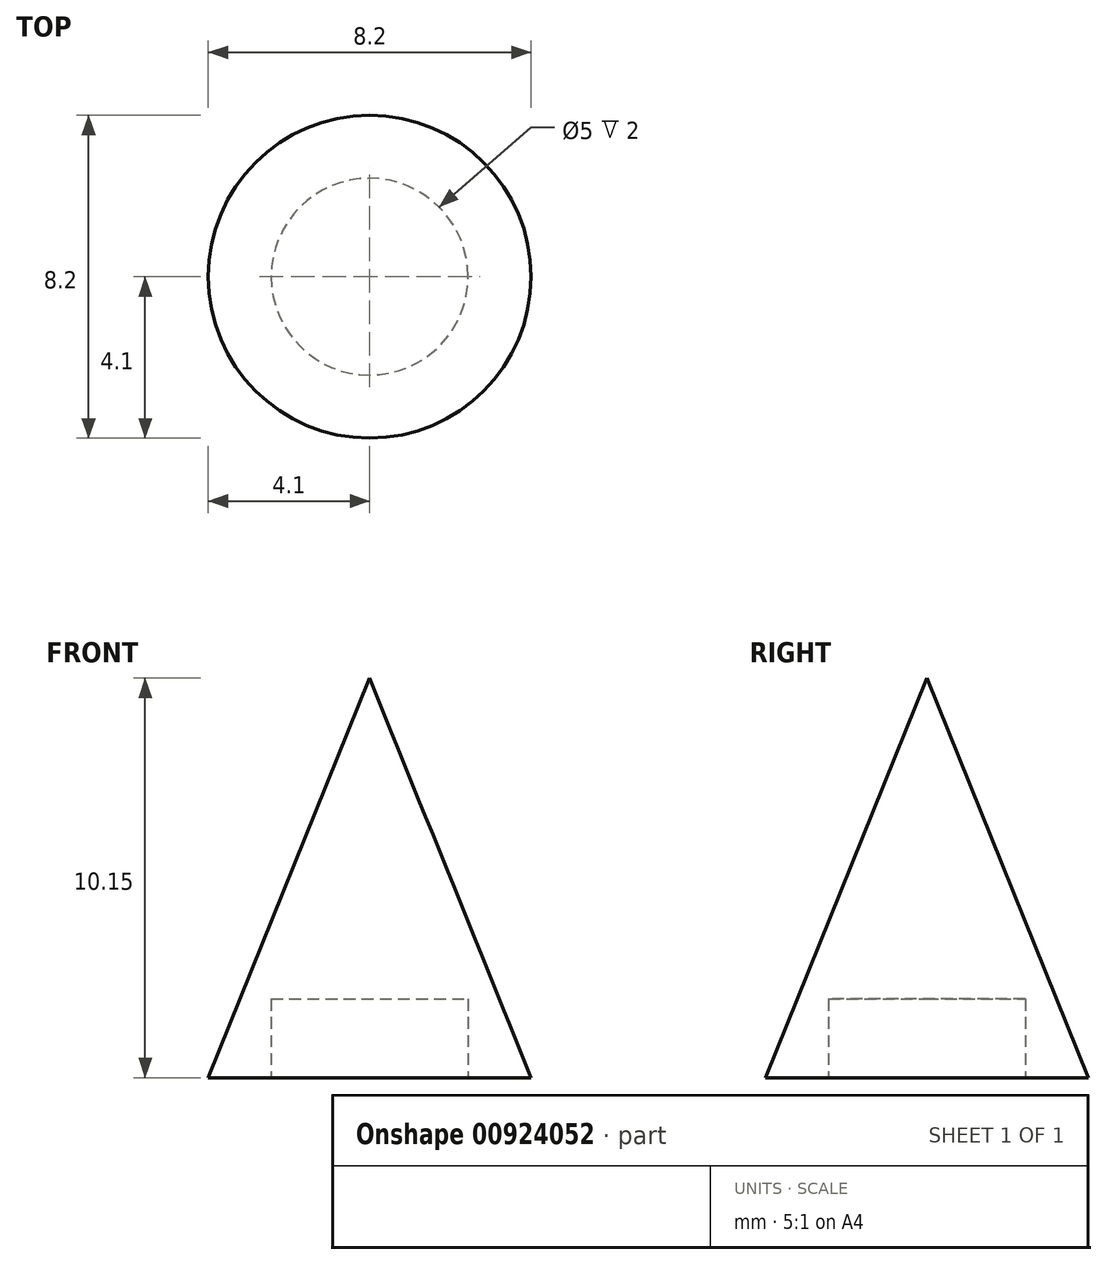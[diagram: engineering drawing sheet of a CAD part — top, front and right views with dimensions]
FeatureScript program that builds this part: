
annotation { "Feature Type Name" : "Feature", "Feature Type Description" : "" }
export const myFeature = defineFeature(function(context is Context, id is Id, definition is map)
    precondition{}
    {
        {
            var Q0;
            Q0=qCreatedBy(makeId("Top.planeOp"),FACE);
            var sketch = newSketch(context, id + "F0", { "sketchPlane" : qUnion([Q0])});
            skCircle(sketch, "E0", {"center": v(0, 0) * mm, "radius": 4.1 * mm});
            skSolve(sketch);
        }
        {
            var Q0;
            Q0 = qSketchRegion(id + "F0", true);
            extrude(context, id + "F1", {"entities" : qUnion([Q0]), "depth" : 12 * mm, "offsetDistance" : 25 * mm, "hasDraft" : true, "draftAngle" : 22 * degree, "draftPullDirection" : true});
        }
        {
            var Q0;
            Q0=makeQuery(id+"F1.opExtrude","CAP_FACE",FACE,{"disambiguationData":[OSD([sQuery(id+"F0.wireOp",EDGE,"E0")])],"isStart":true});
            var sketch = newSketch(context, id + "F2", { "sketchPlane" : qUnion([Q0])});
            skCircle(sketch, "E1", {"center": v(0, 0) * mm, "radius": 2.5 * mm});
            skSolve(sketch);
        }
        {
            var Q0;
            Q0=makeQuery(id+"F2.imprint","IMPRINT",FACE,{"disambiguationData":[TD([[makeQuery(id+"F2.imprint","IMPRINT",EDGE,{"derivedFrom":sQuery(id+"F2.wireOp",EDGE,"E1")}),1.0]])]});
            extrude(context, id + "F3", {"entities" : qUnion([Q0]), "operationType" : NewBodyOperationType.REMOVE, "oppositeDirection" : true, "depth" : 2 * mm, "offsetDistance" : 25 * mm});
        }
    });
